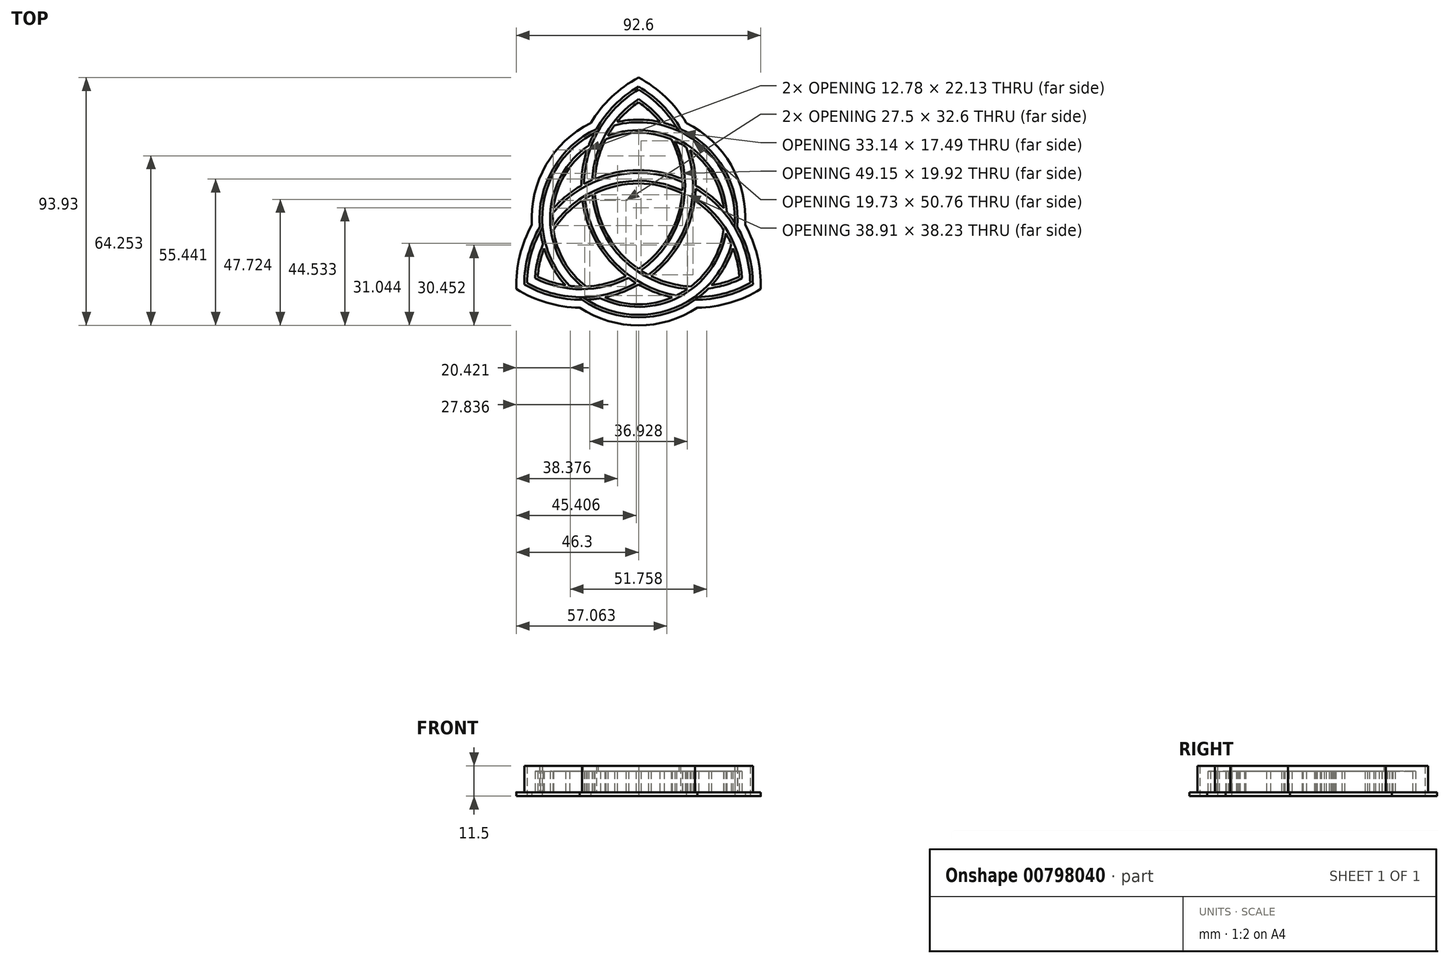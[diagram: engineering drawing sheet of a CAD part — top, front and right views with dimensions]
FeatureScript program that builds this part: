
annotation { "Feature Type Name" : "Feature", "Feature Type Description" : "" }
export const myFeature = defineFeature(function(context is Context, id is Id, definition is map)
    precondition{}
    {
        {
            var Q0;
            Q0=qCreatedBy(makeId("Top.planeOp"),FACE);
            var sketch = newSketch(context, id + "F0", { "sketchPlane" : qUnion([Q0])});
            skCircle(sketch, "E0", {"center": v(0, 0) * mm, "radius": 37.5 * mm});
            skCircle(sketch, "E1", {"center": v(0, 0) * mm, "radius": 36.5 * mm});
            skCircle(sketch, "E2", {"center": v(0, 0) * mm, "radius": 33.5 * mm});
            skCircle(sketch, "E3", {"center": v(0, 0) * mm, "radius": 32.5 * mm});
            skCircle(sketch, "E4", {"center": v(0, 0) * mm, "radius": 50 * mm});
            skLineSegment(sketch, "E5", {"start": v(-43.3, -25) * mm, "end": v(0, 50) * mm});
            skLineSegment(sketch, "E6", {"start": v(0, 50) * mm, "end": v(43.3, -25) * mm});
            skLineSegment(sketch, "E7", {"start": v(43.3, -25) * mm, "end": v(-43.3, -25) * mm});
            skArc(sketch, "E8", {"start": v(-43.3, -25) * mm, "mid": v(15.85, -9.15) * mm, "end": v(0, 50) * mm});
            skArc(sketch, "E9.0", {"start": v(-42.8, -24.13) * mm, "mid": v(14.98, -8.65) * mm, "end": v(-0.5, 49.13) * mm});
            skArc(sketch, "E10.0", {"start": v(-41.3, -21.54) * mm, "mid": v(12.39, -7.15) * mm, "end": v(-2, 46.54) * mm});
            skArc(sketch, "E11.0", {"start": v(-40.8, -20.67) * mm, "mid": v(11.52, -6.65) * mm, "end": v(-2.5, 45.67) * mm});
            skArc(sketch, "E12.1.0", {"start": v(39.3, -25) * mm, "mid": v(0, 14.3) * mm, "end": v(-39.3, -25) * mm});
            skArc(sketch, "E12.1.1", {"start": v(38.3, -25) * mm, "mid": v(0, 13.3) * mm, "end": v(-38.3, -25) * mm});
            skArc(sketch, "E12.1.2", {"start": v(43.3, -25) * mm, "mid": v(0, 18.3) * mm, "end": v(-43.3, -25) * mm});
            skArc(sketch, "E12.1.3", {"start": v(42.3, -25) * mm, "mid": v(0, 17.3) * mm, "end": v(-42.3, -25) * mm});
            skArc(sketch, "E12.2.0", {"start": v(2, 46.54) * mm, "mid": v(-12.39, -7.15) * mm, "end": v(41.3, -21.54) * mm});
            skArc(sketch, "E12.2.1", {"start": v(2.5, 45.67) * mm, "mid": v(-11.52, -6.65) * mm, "end": v(40.8, -20.67) * mm});
            skArc(sketch, "E12.2.2", {"start": v(0, 50) * mm, "mid": v(-15.85, -9.15) * mm, "end": v(43.3, -25) * mm});
            skArc(sketch, "E12.2.3", {"start": v(0.5, 49.13) * mm, "mid": v(-14.98, -8.65) * mm, "end": v(42.8, -24.13) * mm});
            skSolve(sketch);
        }
        {
            var Q0;
            Q0=qCreatedBy(makeId("Top.planeOp"),FACE);
            var sketch = newSketch(context, id + "F1", { "sketchPlane" : qUnion([Q0])});
            skArc(sketch, "E13.0", {"start": v(43.3, -25) * mm, "mid": v(41.8, -13.67) * mm, "end": v(37.37, -3.12) * mm});
            skArc(sketch, "E13.1", {"start": v(-43.3, -25) * mm, "mid": v(-32.73, -29.36) * mm, "end": v(-21.4, -30.8) * mm});
            skArc(sketch, "E13.2", {"start": v(-21.4, -30.8) * mm, "mid": v(0, -37.5) * mm, "end": v(21.4, -30.8) * mm});
            skArc(sketch, "E13.3", {"start": v(0, 50) * mm, "mid": v(-9.06, 43.03) * mm, "end": v(-15.98, 33.93) * mm});
            skArc(sketch, "E14.trimOffspring", {"start": v(-37.37, -3.12) * mm, "mid": v(-41.8, -13.67) * mm, "end": v(-43.3, -25) * mm});
            skArc(sketch, "E15.trimOffspring", {"start": v(21.4, -30.8) * mm, "mid": v(32.73, -29.36) * mm, "end": v(43.3, -25) * mm});
            skArc(sketch, "E16.trimOffspring", {"start": v(15.98, 33.93) * mm, "mid": v(9.06, 43.03) * mm, "end": v(0, 50) * mm});
            skArc(sketch, "E17.trimOffspring", {"start": v(37.37, -3.12) * mm, "mid": v(32.48, 18.75) * mm, "end": v(15.98, 33.93) * mm});
            skArc(sketch, "E18.trimOffspring", {"start": v(-15.98, 33.93) * mm, "mid": v(-32.48, 18.75) * mm, "end": v(-37.37, -3.12) * mm});
            skArc(sketch, "E19.0", {"start": v(15.27, 33.15) * mm, "mid": v(8.66, 42) * mm, "end": v(0, 48.84) * mm});
            skArc(sketch, "E19.1", {"start": v(36.35, -3.36) * mm, "mid": v(31.6, 18.25) * mm, "end": v(15.27, 33.15) * mm});
            skArc(sketch, "E19.2", {"start": v(0, 48.84) * mm, "mid": v(-8.66, 42) * mm, "end": v(-15.27, 33.15) * mm});
            skArc(sketch, "E19.3", {"start": v(42.3, -24.42) * mm, "mid": v(40.7, -13.5) * mm, "end": v(36.35, -3.36) * mm});
            skArc(sketch, "E19.4", {"start": v(21.08, -29.8) * mm, "mid": v(32.04, -28.5) * mm, "end": v(42.3, -24.42) * mm});
            skArc(sketch, "E19.5", {"start": v(-15.27, 33.15) * mm, "mid": v(-31.6, 18.25) * mm, "end": v(-36.35, -3.36) * mm});
            skArc(sketch, "E19.6", {"start": v(-36.35, -3.36) * mm, "mid": v(-40.7, -13.5) * mm, "end": v(-42.3, -24.42) * mm});
            skArc(sketch, "E19.7", {"start": v(-42.3, -24.42) * mm, "mid": v(-32.04, -28.5) * mm, "end": v(-21.08, -29.8) * mm});
            skArc(sketch, "E19.8", {"start": v(-21.08, -29.8) * mm, "mid": v(0, -36.5) * mm, "end": v(21.08, -29.8) * mm});
            skSolve(sketch);
        }
        {
            var Q0;
            Q0 = qSketchRegion(id + "F1", true);
            extrude(context, id + "F2", {"entities" : qUnion([Q0]), "depth" : 11.5 * mm, "offsetDistance" : 25 * mm});
        }
        {
            var Q0;
            Q0=qCreatedBy(makeId("Top.planeOp"),FACE);
            var sketch = newSketch(context, id + "F3", { "sketchPlane" : qUnion([Q0])});
            skArc(sketch, "E20.0", {"start": v(14.4, 34.62) * mm, "mid": v(12.07, 35.5) * mm, "end": v(9.68, 36.23) * mm});
            skArc(sketch, "E20.1", {"start": v(36.46, -1.64) * mm, "mid": v(23.01, 28.33) * mm, "end": v(-9.09, 35.35) * mm});
            skArc(sketch, "E20.2", {"start": v(33.4, 2.56) * mm, "mid": v(18.06, 28.21) * mm, "end": v(-11.66, 31.4) * mm});
            skArc(sketch, "E20.3", {"start": v(12.4, 30.04) * mm, "mid": v(0, 32.5) * mm, "end": v(-12.4, 30.04) * mm});
            skArc(sketch, "E20.8", {"start": v(-43.3, -25) * mm, "mid": v(-32.73, -29.36) * mm, "end": v(-21.4, -30.8) * mm});
            skArc(sketch, "E20.9", {"start": v(-42.3, -24.42) * mm, "mid": v(-21.64, -29.8) * mm, "end": v(-0.99, -24.41) * mm});
            skArc(sketch, "E20.10", {"start": v(-39.23, -22.65) * mm, "mid": v(-21.5, -26.8) * mm, "end": v(-3.82, -22.52) * mm});
            skArc(sketch, "E20.11", {"start": v(-38.19, -22.05) * mm, "mid": v(-33.04, -24.07) * mm, "end": v(-27.65, -25.33) * mm});
            skArc(sketch, "E20.12", {"start": v(39.23, -22.65) * mm, "mid": v(33.96, -5.23) * mm, "end": v(21.41, 7.96) * mm});
            skArc(sketch, "E20.13", {"start": v(38.19, -22.05) * mm, "mid": v(37.36, -16.58) * mm, "end": v(35.76, -11.29) * mm});
            skArc(sketch, "E20.14", {"start": v(43.3, -25) * mm, "mid": v(41.8, -13.67) * mm, "end": v(37.37, -3.12) * mm});
            skArc(sketch, "E20.15", {"start": v(42.3, -24.42) * mm, "mid": v(36.63, -3.84) * mm, "end": v(21.64, 11.35) * mm});
            skArc(sketch, "E20.16", {"start": v(0, 45.3) * mm, "mid": v(-12.46, 32.03) * mm, "end": v(-17.6, 14.56) * mm});
            skArc(sketch, "E20.17", {"start": v(0, 44.1) * mm, "mid": v(-4.32, 40.65) * mm, "end": v(-8.1, 36.61) * mm});
            skArc(sketch, "E20.18", {"start": v(0, 50) * mm, "mid": v(-9.06, 43.03) * mm, "end": v(-15.98, 33.93) * mm});
            skArc(sketch, "E20.19", {"start": v(0, 48.84) * mm, "mid": v(-14.99, 33.64) * mm, "end": v(-20.65, 13.06) * mm});
            skPoint(sketch, "E20.20", {"position": v(0, 0) * mm});
            skArc(sketch, "E21.trimOffspring", {"start": v(9.68, 36.23) * mm, "mid": v(5.22, 41.18) * mm, "end": v(0, 45.3) * mm});
            skArc(sketch, "E22.trimOffspring", {"start": v(8.1, 36.61) * mm, "mid": v(4.32, 40.65) * mm, "end": v(0, 44.1) * mm});
            skArc(sketch, "E23.trimOffspring", {"start": v(14.4, 34.62) * mm, "mid": v(8.07, 42.6) * mm, "end": v(0, 48.84) * mm});
            skArc(sketch, "E24.trimOffspring", {"start": v(15.98, 33.93) * mm, "mid": v(9.06, 43.03) * mm, "end": v(0, 50) * mm});
            skArc(sketch, "E25.trimOffspring", {"start": v(8.1, 36.61) * mm, "mid": v(0, 37.5) * mm, "end": v(-8.1, 36.61) * mm});
            skArc(sketch, "E26.trimOffspring", {"start": v(18.09, 27) * mm, "mid": v(16, 28.29) * mm, "end": v(13.83, 29.41) * mm});
            skArc(sketch, "E27.trimOffspring", {"start": v(32.27, 3.88) * mm, "mid": v(28.15, 16.25) * mm, "end": v(19.49, 26) * mm});
            skArc(sketch, "E28.trimOffspring", {"start": v(37.37, -3.12) * mm, "mid": v(32.48, 18.75) * mm, "end": v(15.98, 33.93) * mm});
            skArc(sketch, "E29.trimOffspring", {"start": v(36.46, -1.64) * mm, "mid": v(35, 0.5) * mm, "end": v(33.4, 2.56) * mm});
            skArc(sketch, "E30.trimOffspring", {"start": v(32.27, 3.88) * mm, "mid": v(27.3, 8.6) * mm, "end": v(21.65, 12.5) * mm});
            skArc(sketch, "E31.trimOffspring", {"start": v(32.22, -4.29) * mm, "mid": v(27.32, 1.84) * mm, "end": v(21.28, 6.85) * mm});
            skArc(sketch, "E32.trimOffspring", {"start": v(35.16, -9.8) * mm, "mid": v(34.16, -7.67) * mm, "end": v(33.03, -5.6) * mm});
            skArc(sketch, "E33.trimOffspring", {"start": v(27.65, -25.33) * mm, "mid": v(33.04, -24.07) * mm, "end": v(38.19, -22.05) * mm});
            skArc(sketch, "E34.trimOffspring", {"start": v(26.54, -26.5) * mm, "mid": v(33.05, -25.11) * mm, "end": v(39.23, -22.65) * mm});
            skArc(sketch, "E35.trimOffspring", {"start": v(22.78, -29.79) * mm, "mid": v(32.87, -28.29) * mm, "end": v(42.3, -24.42) * mm});
            skArc(sketch, "E36.trimOffspring", {"start": v(21.4, -30.8) * mm, "mid": v(32.73, -29.36) * mm, "end": v(43.3, -25) * mm});
            skArc(sketch, "E37.trimOffspring", {"start": v(22.78, -29.79) * mm, "mid": v(24.71, -28.2) * mm, "end": v(26.54, -26.5) * mm});
            skArc(sketch, "E38.trimOffspring", {"start": v(27.65, -25.33) * mm, "mid": v(32.48, -18.75) * mm, "end": v(35.76, -11.29) * mm});
            skArc(sketch, "E39.trimOffspring", {"start": v(19.82, -25.76) * mm, "mid": v(28.15, -16.25) * mm, "end": v(32.22, -4.29) * mm});
            skArc(sketch, "E40.trimOffspring", {"start": v(14.34, -29.16) * mm, "mid": v(16.5, -28) * mm, "end": v(18.56, -26.68) * mm});
            skArc(sketch, "E41.trimOffspring", {"start": v(-19.66, -30.76) * mm, "mid": v(13.03, -34.1) * mm, "end": v(35.16, -9.8) * mm});
            skArc(sketch, "E42.trimOffspring", {"start": v(-21.4, -30.8) * mm, "mid": v(0, -37.5) * mm, "end": v(21.4, -30.8) * mm});
            skArc(sketch, "E43.trimOffspring", {"start": v(-14.49, -30.2) * mm, "mid": v(15.4, -29.75) * mm, "end": v(33.03, -5.6) * mm});
            skArc(sketch, "E44.trimOffspring", {"start": v(-12.78, -29.88) * mm, "mid": v(0, -32.5) * mm, "end": v(12.78, -29.88) * mm});
            skArc(sketch, "E45.trimOffspring", {"start": v(-12.78, -29.88) * mm, "mid": v(-6.2, -27.95) * mm, "end": v(0, -25) * mm});
            skArc(sketch, "E46.trimOffspring", {"start": v(-19.66, -30.76) * mm, "mid": v(-17.06, -30.56) * mm, "end": v(-14.49, -30.2) * mm});
            skArc(sketch, "E47.trimOffspring", {"start": v(-19.82, -25.76) * mm, "mid": v(-12.06, -24.58) * mm, "end": v(-4.71, -21.85) * mm});
            skArc(sketch, "E48.trimOffspring", {"start": v(-26.07, -25.55) * mm, "mid": v(-23.72, -25.75) * mm, "end": v(-21.37, -25.8) * mm});
            skArc(sketch, "E49.trimOffspring", {"start": v(-36.21, -9.73) * mm, "mid": v(-38.27, -16.06) * mm, "end": v(-39.23, -22.65) * mm});
            skArc(sketch, "E50.trimOffspring", {"start": v(-35.76, -11.29) * mm, "mid": v(-37.36, -16.58) * mm, "end": v(-38.19, -22.05) * mm});
            skArc(sketch, "E51.trimOffspring", {"start": v(-37.19, -4.84) * mm, "mid": v(-40.93, -14.32) * mm, "end": v(-42.3, -24.42) * mm});
            skArc(sketch, "E52.trimOffspring", {"start": v(-37.37, -3.12) * mm, "mid": v(-41.8, -13.67) * mm, "end": v(-43.3, -25) * mm});
            skArc(sketch, "E53.trimOffspring", {"start": v(-32.43, 2.16) * mm, "mid": v(-32.5, -0.29) * mm, "end": v(-32.38, -2.73) * mm});
            skArc(sketch, "E54.trimOffspring", {"start": v(-32.22, -4.29) * mm, "mid": v(-28.15, -16.25) * mm, "end": v(-19.82, -25.76) * mm});
            skArc(sketch, "E55.trimOffspring", {"start": v(-35.76, -11.29) * mm, "mid": v(-32.48, -18.75) * mm, "end": v(-27.65, -25.33) * mm});
            skArc(sketch, "E56.trimOffspring", {"start": v(-37.19, -4.84) * mm, "mid": v(-36.78, -7.3) * mm, "end": v(-36.21, -9.73) * mm});
            skArc(sketch, "E57.trimOffspring", {"start": v(-19.49, 26) * mm, "mid": v(-28.15, 16.25) * mm, "end": v(-32.27, 3.88) * mm});
            skArc(sketch, "E58.trimOffspring", {"start": v(-18.91, 27.65) * mm, "mid": v(-33.46, 1.54) * mm, "end": v(-21.37, -25.8) * mm});
            skArc(sketch, "E59.trimOffspring", {"start": v(-16.8, 32.4) * mm, "mid": v(-36.04, 5.76) * mm, "end": v(-26.07, -25.55) * mm});
            skArc(sketch, "E60.trimOffspring", {"start": v(-15.98, 33.93) * mm, "mid": v(-32.48, 18.75) * mm, "end": v(-37.37, -3.12) * mm});
            skArc(sketch, "E61.trimOffspring", {"start": v(-16.8, 32.4) * mm, "mid": v(-17.93, 30.06) * mm, "end": v(-18.91, 27.65) * mm});
            skArc(sketch, "E62.trimOffspring", {"start": v(-19.49, 26) * mm, "mid": v(-21.1, 19.34) * mm, "end": v(-21.65, 12.5) * mm});
            skArc(sketch, "E63.trimOffspring", {"start": v(-12.4, 30.04) * mm, "mid": v(-15.26, 22.74) * mm, "end": v(-16.57, 15) * mm});
            skArc(sketch, "E64.trimOffspring", {"start": v(-9.09, 35.35) * mm, "mid": v(-10.43, 33.42) * mm, "end": v(-11.66, 31.4) * mm});
            skArc(sketch, "E65.trimOffspring", {"start": v(16.57, 15) * mm, "mid": v(0, 18.3) * mm, "end": v(-16.57, 15) * mm});
            skArc(sketch, "E66.trimOffspring", {"start": v(16.63, 13.9) * mm, "mid": v(-9.84, 16.14) * mm, "end": v(-32.43, 2.16) * mm});
            skArc(sketch, "E67.trimOffspring", {"start": v(16.6, 10.62) * mm, "mid": v(-10.34, 12.92) * mm, "end": v(-32.38, -2.73) * mm});
            skArc(sketch, "E68.trimOffspring", {"start": v(16.54, 9.55) * mm, "mid": v(0, 13.3) * mm, "end": v(-16.54, 9.55) * mm});
            skArc(sketch, "E69.trimOffspring", {"start": v(21.41, 7.96) * mm, "mid": v(21.56, 9.65) * mm, "end": v(21.64, 11.35) * mm});
            skArc(sketch, "E70.trimOffspring", {"start": v(21.65, 12.5) * mm, "mid": v(21.1, 19.34) * mm, "end": v(19.49, 26) * mm});
            skArc(sketch, "E71.trimOffspring", {"start": v(16.57, 15) * mm, "mid": v(15.26, 22.74) * mm, "end": v(12.4, 30.04) * mm});
            skArc(sketch, "E72.trimOffspring", {"start": v(16.6, 10.62) * mm, "mid": v(16.65, 12.26) * mm, "end": v(16.63, 13.9) * mm});
            skArc(sketch, "E73.trimOffspring", {"start": v(4.71, -21.85) * mm, "mid": v(15.85, -9.15) * mm, "end": v(21.28, 6.85) * mm});
            skArc(sketch, "E74.trimOffspring", {"start": v(3.72, -21.35) * mm, "mid": v(18.9, 0.45) * mm, "end": v(18.09, 27) * mm});
            skArc(sketch, "E75.trimOffspring", {"start": v(0.9, -19.7) * mm, "mid": v(16.36, 2.5) * mm, "end": v(13.83, 29.41) * mm});
            skArc(sketch, "E76.trimOffspring", {"start": v(0, -19.1) * mm, "mid": v(11.52, -6.65) * mm, "end": v(16.54, 9.55) * mm});
            skArc(sketch, "E77.trimOffspring", {"start": v(0.9, -19.7) * mm, "mid": v(2.3, -20.55) * mm, "end": v(3.72, -21.35) * mm});
            skArc(sketch, "E78.trimOffspring", {"start": v(4.71, -21.85) * mm, "mid": v(12.06, -24.58) * mm, "end": v(19.82, -25.76) * mm});
            skArc(sketch, "E79.trimOffspring", {"start": v(0, -25) * mm, "mid": v(6.2, -27.95) * mm, "end": v(12.78, -29.88) * mm});
            skArc(sketch, "E80.trimOffspring", {"start": v(-3.82, -22.52) * mm, "mid": v(-2.42, -23.5) * mm, "end": v(-0.99, -24.41) * mm});
            skArc(sketch, "E81.trimOffspring", {"start": v(-21.28, 6.85) * mm, "mid": v(-15.85, -9.15) * mm, "end": v(-4.71, -21.85) * mm});
            skArc(sketch, "E82.trimOffspring", {"start": v(-20.35, 7.45) * mm, "mid": v(-9.06, -16.6) * mm, "end": v(14.34, -29.16) * mm});
            skArc(sketch, "E83.trimOffspring", {"start": v(-17.5, 9.07) * mm, "mid": v(-6.02, -15.41) * mm, "end": v(18.56, -26.68) * mm});
            skArc(sketch, "E84.trimOffspring", {"start": v(-16.54, 9.55) * mm, "mid": v(-11.52, -6.65) * mm, "end": v(0, -19.1) * mm});
            skArc(sketch, "E85.trimOffspring", {"start": v(-17.5, 9.07) * mm, "mid": v(-18.94, 8.29) * mm, "end": v(-20.35, 7.45) * mm});
            skArc(sketch, "E86.trimOffspring", {"start": v(-21.28, 6.85) * mm, "mid": v(-27.32, 1.84) * mm, "end": v(-32.22, -4.29) * mm});
            skArc(sketch, "E87.trimOffspring", {"start": v(-21.65, 12.5) * mm, "mid": v(-27.3, 8.6) * mm, "end": v(-32.27, 3.88) * mm});
            skArc(sketch, "E88.trimOffspring", {"start": v(-17.6, 14.56) * mm, "mid": v(-19.14, 13.84) * mm, "end": v(-20.65, 13.06) * mm});
            skSolve(sketch);
        }
        {
            var Q0;
            Q0 = qSketchRegion(id + "F3", true);
            extrude(context, id + "F4", {"entities" : qUnion([Q0]), "operationType" : NewBodyOperationType.ADD, "depth" : (8 + 1.5) * mm, "offsetDistance" : 25 * mm});
        }
        {
            var Q0;
            Q0=qCreatedBy(makeId("Top.planeOp"),FACE);
            var sketch = newSketch(context, id + "F5", { "sketchPlane" : qUnion([Q0])});
            skArc(sketch, "E89.0.0", {"start": v(-15.98, 33.93) * mm, "mid": v(-9.06, 43.03) * mm, "end": v(0, 50) * mm});
            skArc(sketch, "E89.0.2", {"start": v(-43.3, -25) * mm, "mid": v(-41.8, -13.67) * mm, "end": v(-37.37, -3.12) * mm});
            skArc(sketch, "E89.0.3", {"start": v(-37.37, -3.12) * mm, "mid": v(-32.48, 18.75) * mm, "end": v(-15.98, 33.93) * mm});
            skArc(sketch, "E89.1.0", {"start": v(37.37, -3.12) * mm, "mid": v(41.8, -13.67) * mm, "end": v(43.3, -25) * mm});
            skArc(sketch, "E89.1.2", {"start": v(0, 50) * mm, "mid": v(9.06, 43.03) * mm, "end": v(15.98, 33.93) * mm});
            skArc(sketch, "E89.1.3", {"start": v(15.98, 33.93) * mm, "mid": v(32.48, 18.75) * mm, "end": v(37.37, -3.12) * mm});
            skArc(sketch, "E89.2.0", {"start": v(21.4, -30.8) * mm, "mid": v(0, -37.5) * mm, "end": v(-21.4, -30.8) * mm});
            skArc(sketch, "E89.2.1", {"start": v(-21.4, -30.8) * mm, "mid": v(-32.73, -29.36) * mm, "end": v(-43.3, -25) * mm});
            skArc(sketch, "E89.2.3", {"start": v(43.3, -25) * mm, "mid": v(32.73, -29.36) * mm, "end": v(21.4, -30.8) * mm});
            skArc(sketch, "E90.0", {"start": v(46.27, -26.71) * mm, "mid": v(45.02, -14.17) * mm, "end": v(40.43, -2.43) * mm});
            skArc(sketch, "E90.1", {"start": v(18.11, 36.23) * mm, "mid": v(35.07, 20.25) * mm, "end": v(40.43, -2.43) * mm});
            skArc(sketch, "E90.2", {"start": v(46.27, -26.71) * mm, "mid": v(34.78, -31.9) * mm, "end": v(22.32, -33.8) * mm});
            skArc(sketch, "E90.3", {"start": v(0, 53.43) * mm, "mid": v(10.24, 46.07) * mm, "end": v(18.11, 36.23) * mm});
            skArc(sketch, "E90.4", {"start": v(-18.11, 36.23) * mm, "mid": v(-10.24, 46.07) * mm, "end": v(0, 53.43) * mm});
            skArc(sketch, "E90.5", {"start": v(22.32, -33.8) * mm, "mid": v(0, -40.5) * mm, "end": v(-22.32, -33.8) * mm});
            skArc(sketch, "E90.6", {"start": v(-22.32, -33.8) * mm, "mid": v(-34.78, -31.9) * mm, "end": v(-46.27, -26.71) * mm});
            skArc(sketch, "E90.7", {"start": v(-46.27, -26.71) * mm, "mid": v(-45.02, -14.17) * mm, "end": v(-40.43, -2.43) * mm});
            skArc(sketch, "E90.8", {"start": v(-40.43, -2.43) * mm, "mid": v(-35.07, 20.25) * mm, "end": v(-18.11, 36.23) * mm});
            skSolve(sketch);
        }
        {
            var Q0;
            Q0 = qSketchRegion(id + "F5", true);
            extrude(context, id + "F6", {"entities" : qUnion([Q0]), "operationType" : NewBodyOperationType.ADD, "depth" : 1.5 * mm, "offsetDistance" : 25 * mm});
        }
    });
